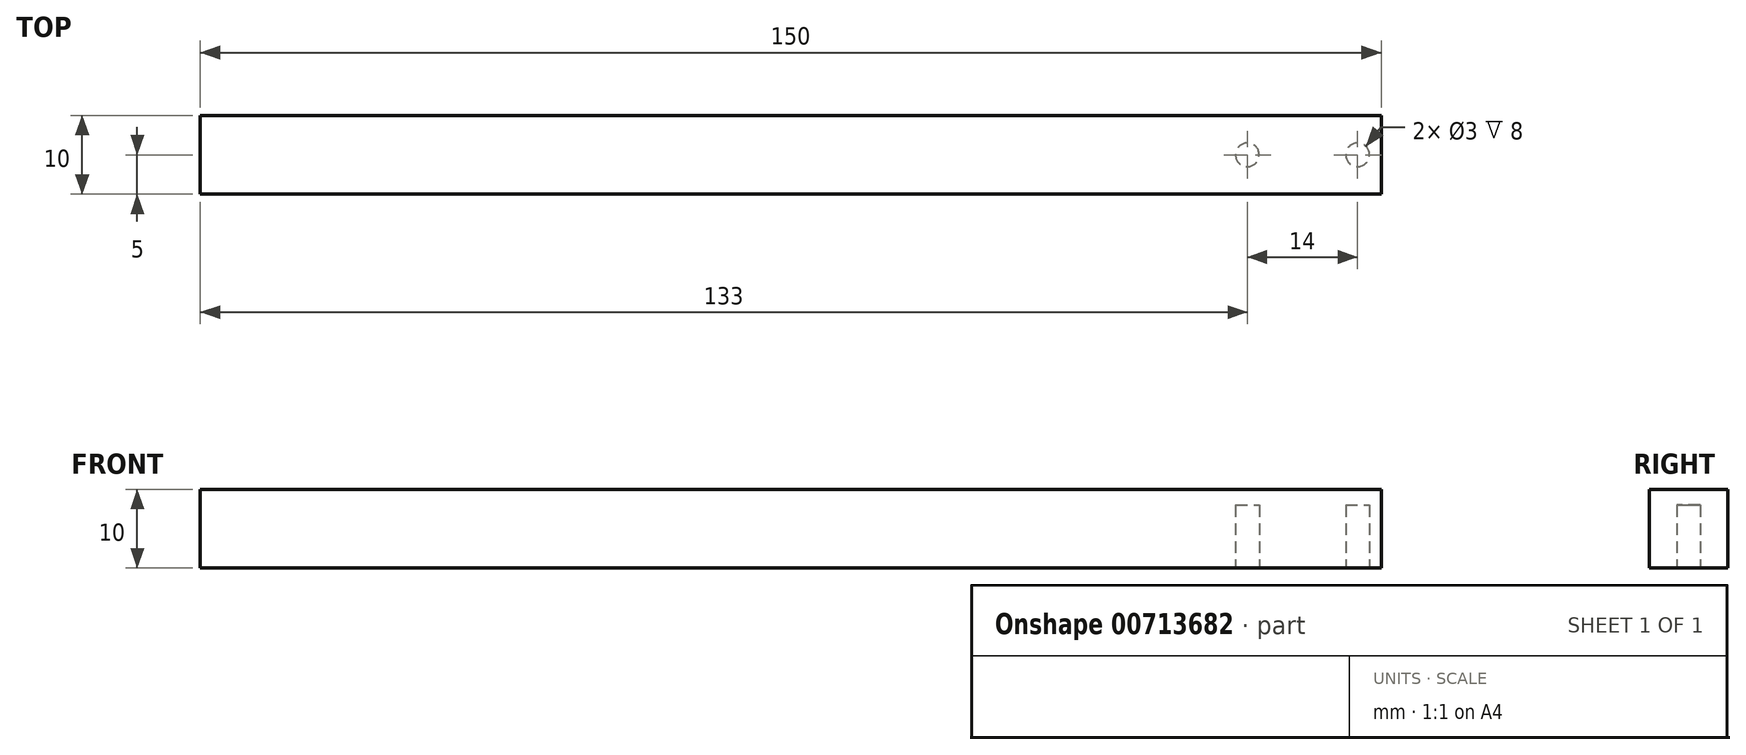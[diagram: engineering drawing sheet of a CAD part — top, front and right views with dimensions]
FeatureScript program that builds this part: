
annotation { "Feature Type Name" : "Feature", "Feature Type Description" : "" }
export const myFeature = defineFeature(function(context is Context, id is Id, definition is map)
    precondition{}
    {
        {
            var Q0;
            Q0=qCreatedBy(makeId("Front.planeOp"),FACE);
            var sketch = newSketch(context, id + "F0", { "sketchPlane" : qUnion([Q0])});
            skLineSegment(sketch, "E0.bottom", {"start": v(75, -5) * mm, "end": v(-75, -5) * mm});
            skLineSegment(sketch, "E0.top", {"start": v(75, 5) * mm, "end": v(-75, 5) * mm});
            skLineSegment(sketch, "E0.left", {"start": v(75, -5) * mm, "end": v(75, 5) * mm});
            skLineSegment(sketch, "E0.right", {"start": v(-75, -5) * mm, "end": v(-75, 5) * mm});
            skPoint(sketch, "E0.middle", {"position": v(0, 0) * mm});
            skSolve(sketch);
        }
        {
            var Q0;
            Q0=makeQuery(id+"F0.imprint","IMPRINT",FACE,{"disambiguationData":[TD([[makeQuery(id+"F0.imprint","IMPRINT",EDGE,{"derivedFrom":sQuery(id+"F0.wireOp",EDGE,"E0.bottom")}),-1.0]])]});
            extrude(context, id + "F1", {"entities" : qUnion([Q0]), "endBound" : BoundingType.SYMMETRIC, "depth" : 10 * mm, "offsetDistance" : 25 * mm});
        }
        {
            var Q0;
            Q0=makeQuery(id+"F1.opExtrude","SWEPT_FACE",FACE,{"disambiguationData":[OSD([sQuery(id+"F0.wireOp",EDGE,"E0.bottom")])]});
            var sketch = newSketch(context, id + "F2", { "sketchPlane" : qUnion([Q0])});
            skCircle(sketch, "E1", {"center": v(72, 0) * mm, "radius": 1.5 * mm});
            skCircle(sketch, "E2", {"center": v(58, 0) * mm, "radius": 1.5 * mm});
            skSolve(sketch);
        }
        {
            var Q0;
            Q0=makeQuery(id+"F2.imprint","IMPRINT",FACE,{"disambiguationData":[TD([[makeQuery(id+"F2.imprint","IMPRINT",EDGE,{"derivedFrom":sQuery(id+"F2.wireOp",EDGE,"E1")}),1.0]])]});
            var Q1;
            Q1=makeQuery(id+"F2.imprint","IMPRINT",FACE,{"disambiguationData":[TD([[makeQuery(id+"F2.imprint","IMPRINT",EDGE,{"derivedFrom":sQuery(id+"F2.wireOp",EDGE,"E2")}),1.0]])]});
            extrude(context, id + "F3", {"entities" : qUnion([Q0, Q1]), "operationType" : NewBodyOperationType.REMOVE, "oppositeDirection" : true, "depth" : 8 * mm, "offsetDistance" : 25 * mm});
        }
    });
